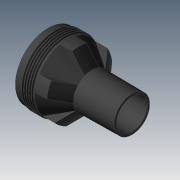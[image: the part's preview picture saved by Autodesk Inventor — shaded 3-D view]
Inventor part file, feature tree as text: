
AUTODESK INVENTOR PART (.ipt)
format: ipt  version: 2020 (Build 240168000, 168)  size: 325,120 bytes
history: native  units: mm
features: sketch x3, chamfer x2, revolve x1, plane x1, extrude x1, pattern_circular x1, helix x1
ambient origin geometry x8: Origin, YZ Plane, XZ Plane, XY Plane, X Axis, Y Axis, Z Axis, Center Point
bodies: Solid1 (feature_tree)
feature tree (10):
  revolve  "Revolution1"  [1 undecoded]
  plane  "Work Plane1"
  extrude  "Extrusion1"  TaperAngle=90.0deg  [1 undecoded]
  chamfer  "Chamfer1"  Angle=90.0deg  [1 undecoded]
  pattern_circular  "Circular Pattern1"  [2 undecoded]
  helix  "Coil1"  [1 undecoded]
  chamfer  "Chamfer2"  Distance=20.25mm
  sketch  "Sketch1"  dims[d0=11.0mm d1=25.0mm]
  sketch  "Sketch2"  dims[d2=11.25mm d3=90.0deg]
  sketch  "Sketch3"  dims[d4=1.5mm d5=90.0deg d7=3.5mm d8=15.0mm d9=20.25mm d10=12.0mm d11=90.0deg d12=-25.0mm d13=9.0mm d14=10.0mm d15=0.0mm d16=9.0mm d17=9.0mm d18=6.981317mm d19=50.0mm d20=360.0deg d22=1.5mm d23=1.0mm d24=0.75mm d25=0.15mm d26=0.1mm d27=1.5mm d28=7.5mm d29=10.0mm d30=0.0mm d31=90.0deg d32=90.0deg d33=0.0mm d34=0.0mm d35=0.44mm d36=9.0mm d37=6.981317mm]
note: 6 required parameter values undecoded (feature->parameter linkage not recoverable at this tier; creation-order binding heuristic only, values carry confidence <= 0.55)